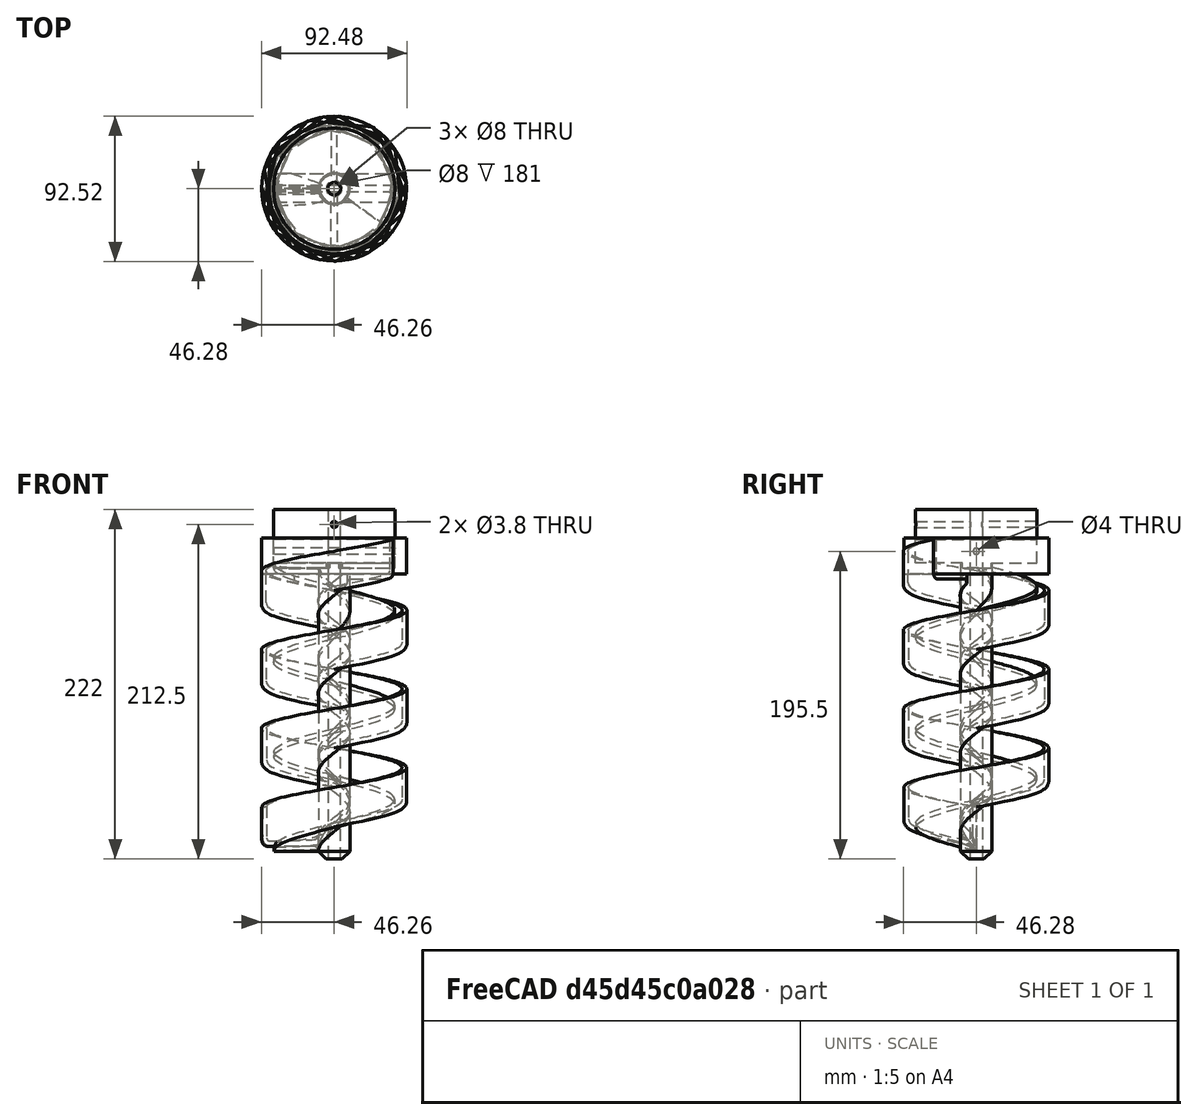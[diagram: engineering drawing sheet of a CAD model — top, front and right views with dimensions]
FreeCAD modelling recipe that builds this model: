
FCSTD DOCUMENT  (FreeCAD 1.1R14555 (Git shallow))
Label: Body - 1.4
License: All rights reserved
LicenseURL: https://en.wikipedia.org/wiki/All_rights_reserved
objects: Sketcher::SketchObject×13, PartDesign::Pad×7, PartDesign::Chamfer×6, PartDesign::Pocket×5, PartDesign::AdditiveHelix×2, PartDesign::Body×2, App::Point×2, PartDesign::Fillet×1
note: 91 computed .brp shape members not serialized (recipe doc carries the construction recipe); baked Part::Feature solids carry a one-line shape summary decoded from their .brp

FEATURE [Sketcher::SketchObject] Sketch
  ArcFitTolerance = 1e-06
  AttachmentSupport = -> [XY_Plane]
  ExternalTypes = [0]
  FullyConstrained = true
  MakeInternals = false
  MapMode = 5
  sketch-geometry (1):
    g0: Circle CenterX=0 CenterY=0 CenterZ=0 NormalX=0 NormalY=0 NormalZ=1 AngleXU=0 Radius=10
  constraints (2):
    c: Coincident(g0,g-1)
    c: Diameter(g0) = 20
FEATURE [PartDesign::Pad] Pad
  Direction = (0,0,1)
  Length = 200
  Length2 = 10
  Profile = -> Sketch
  ReferenceAxis = -> Sketch [N_Axis]
  Refine = true
  SideType = 0
  Suppressed = false
  Type = 0
  Type2 = 0
FEATURE [PartDesign::Chamfer] Chamfer
  Angle = 45
  Base = -> Pad [Edge2]
  BaseFeature = -> Pad
  ChamferType = 0
  FlipDirection = false
  Refine = true
  Size = 5
  Size2 = 1
  SupportTransform = false
  Suppressed = false
  UseAllEdges = false
FEATURE [Sketcher::SketchObject] Sketch001
  ArcFitTolerance = 1e-06
  AttachmentSupport = -> [XZ_Plane]
  ExternalGeometry = -> [Chamfer]
  ExternalTypes = [0]
  FullyConstrained = true
  MakeInternals = false
  MapMode = 5
  Placement = pos=(0,0,0) rot=(1,0,0;1.5708rad)
  expr: Constraints[11] = 77 / 2 - 0.3
  sketch-geometry (4):
    g0: LineSegment StartX=-38.2 StartY=8 StartZ=0 EndX=-38.2 EndY=5 EndZ=0
    g1: LineSegment StartX=-38.2 StartY=5 StartZ=0 EndX=0 EndY=5 EndZ=0
    g2: LineSegment StartX=0 StartY=5 StartZ=0 EndX=0 EndY=8 EndZ=0
    g3: LineSegment StartX=0 StartY=8 StartZ=0 EndX=-38.2 EndY=8 EndZ=0
  constraints (12):
    c: Coincident(g0,g1)
    c: Coincident(g1,g2)
    c: Coincident(g2,g3)
    c: Coincident(g3,g0)
    c: Vertical(g0)
    c: Vertical(g2)
    c: Horizontal(g1)
    c: Horizontal(g3)
    c: PointOnObject(g1,g-2)
    c: Horizontal(g0,g-3)
    c: DistanceY(g0,g0) = 3
    c: DistanceX(g1,g1) = 38.2
FEATURE [PartDesign::AdditiveHelix] AdditiveHelix
  Angle = 0.1
  Axis = (0,2e-16,1)
  Base = (0,0,0)
  BaseFeature = -> Chamfer
  Growth = 0.10472
  HasBeenEdited = true
  Height = 180
  LeftHanded = false
  Mode = 0
  Outside = false
  Pitch = 60
  Profile = -> Sketch001
  ReferenceAxis = -> Sketch001 [V_Axis]
  Refine = true
  Suppressed = false
  Tolerance = 0.1
  Turns = 3
FEATURE [Sketcher::SketchObject] Sketch002
  ArcFitTolerance = 1e-06
  AttachmentSupport = -> [Chamfer]
  ExternalTypes = [0]
  FullyConstrained = true
  MakeInternals = false
  MapMode = 5
  Placement = pos=(0,0,200) rot=(0,0,1;0rad)
  sketch-geometry (1):
    g0: Circle CenterX=0 CenterY=0 CenterZ=0 NormalX=0 NormalY=0 NormalZ=1 AngleXU=0 Radius=38.5
  constraints (2):
    c: Coincident(g0,g-1)
    c: Diameter(g0) = 77
FEATURE [PartDesign::Chamfer] Chamfer001
  Angle = 45
  Base = -> AdditiveHelix [Edge12]
  BaseFeature = -> AdditiveHelix
  ChamferType = 0
  FlipDirection = false
  Refine = true
  Size = 2.99
  Size2 = 1
  SupportTransform = false
  Suppressed = false
  UseAllEdges = false
FEATURE [PartDesign::Chamfer] Chamfer002
  Angle = 45
  Base = -> Chamfer001 [Edge12]
  BaseFeature = -> Chamfer001
  ChamferType = 0
  FlipDirection = false
  Refine = true
  Size = 4
  Size2 = 1
  SupportTransform = false
  Suppressed = false
  UseAllEdges = false
FEATURE [PartDesign::Chamfer] Chamfer003
  Angle = 45
  Base = -> Chamfer002 [Edge13]
  BaseFeature = -> Chamfer002
  ChamferType = 0
  FlipDirection = false
  Refine = true
  Size = 4
  Size2 = 1
  SupportTransform = false
  Suppressed = false
  UseAllEdges = false
FEATURE [PartDesign::Pad] Pad001
  BaseFeature = -> Chamfer003
  Direction = (0,0,1)
  Length = 3
  Length2 = 10
  Profile = -> Sketch002
  ReferenceAxis = -> Sketch002 [N_Axis]
  Refine = true
  SideType = 0
  Suppressed = false
  Type = 0
  Type2 = 0
FEATURE [Sketcher::SketchObject] Sketch003
  ArcFitTolerance = 1e-06
  AttachmentSupport = -> [Pad001]
  ExternalTypes = [0]
  FullyConstrained = true
  MakeInternals = false
  MapMode = 5
  Placement = pos=(0,0,200) rot=(1,0,0;3.14159rad)
  sketch-geometry (1):
    g0: Circle CenterX=0 CenterY=0 CenterZ=0 NormalX=0 NormalY=0 NormalZ=1 AngleXU=0 Radius=38.5
  constraints (2):
    c: Coincident(g0,g-1)
    c: Diameter(g0) = 77
FEATURE [PartDesign::Pad] Pad002
  BaseFeature = -> Pad001
  Direction = (0,0,-1)
  Length = 12
  Length2 = 10
  Profile = -> Sketch003
  ReferenceAxis = -> Sketch003 [N_Axis]
  Refine = true
  SideType = 0
  Suppressed = false
  Type = 0
  Type2 = 0
FEATURE [PartDesign::Fillet] Fillet
  Base = -> Pad002 [Edge36]
  BaseFeature = -> Pad002
  Radius = 3
  Refine = true
  SupportTransform = false
  Suppressed = false
  UseAllEdges = false
FEATURE [Sketcher::SketchObject] Sketch004
  ArcFitTolerance = 1e-06
  AttachmentSupport = -> [Fillet]
  ExternalTypes = [0]
  FullyConstrained = true
  MakeInternals = false
  MapMode = 5
  Placement = pos=(0,0,203) rot=(0,0,1;0rad)
  sketch-geometry (2):
    g0: Circle CenterX=0 CenterY=0 CenterZ=0 NormalX=0 NormalY=0 NormalZ=1 AngleXU=0 Radius=38.5
    g1: Circle CenterX=0 CenterY=0 CenterZ=0 NormalX=0 NormalY=0 NormalZ=1 AngleXU=0 Radius=50
  constraints (4):
    c: Coincident(g0,g-1)
    c: Diameter(g0) = 77
    c: Coincident(g1,g0)
    c: Diameter(g1) = 100
FEATURE [PartDesign::Pocket] Pocket
  BaseFeature = -> Fillet
  Direction = (0,0,-1)
  Length = 180
  Length2 = 5
  Profile = -> Sketch004
  ReferenceAxis = -> Sketch004 [N_Axis]
  Refine = true
  Reversed = true
  SideType = 0
  Suppressed = false
  Type = 0
  Type2 = 0
FEATURE [Sketcher::SketchObject] Sketch005
  ArcFitTolerance = 1e-06
  AttachmentSupport = -> [YZ_Plane]
  ExternalGeometry = -> [Pocket]
  ExternalTypes = [0]
  FullyConstrained = true
  MakeInternals = false
  MapMode = 5
  Placement = pos=(0,0,0) rot=(0.57735,0.57735,0.57735;2.0944rad)
  sketch-geometry (1):
    g0: Circle CenterX=9.4e-15 CenterY=195.5 CenterZ=0 NormalX=0 NormalY=0 NormalZ=1 AngleXU=0 Radius=2
  constraints (3):
    c: PointOnObject(g0,g-3)
    c: Diameter(g0) = 4
    c: Symmetric(g-3,g-3,g0)
FEATURE [PartDesign::Pocket] Pocket001
  BaseFeature = -> Pocket
  Direction = (-1,0,0)
  Length = 500
  Length2 = 5
  Profile = -> Sketch005
  ReferenceAxis = -> Sketch005 [N_Axis]
  Refine = true
  Reversed = true
  SideType = 0
  Suppressed = false
  Type = 0
  Type2 = 0
FEATURE [PartDesign::Pocket] Pocket002
  BaseFeature = -> Pocket001
  Direction = (-1,0,0)
  Length = 5
  Length2 = 5
  Profile = -> Pocket001 [Face21]
  Refine = true
  SideType = 0
  Suppressed = false
  Type = 1
  Type2 = 0
FEATURE [Sketcher::SketchObject] Sketch006
  ArcFitTolerance = 1e-06
  AttachmentSupport = -> [YZ_Plane]
  ExternalTypes = [0]
  FullyConstrained = false
  MakeInternals = false
  MapMode = 5
  Placement = pos=(0,0,0) rot=(0.57735,0.57735,0.57735;2.0944rad)
  sketch-geometry (4):
    g0: LineSegment StartX=9.56195 StartY=192.563 StartZ=0 EndX=-8.62475 EndY=192.563 EndZ=0
    g1: LineSegment StartX=-8.62475 StartY=192.563 StartZ=0 EndX=-8.62475 EndY=184.759 EndZ=0
    g2: LineSegment StartX=-8.62475 StartY=184.759 StartZ=0 EndX=9.56195 EndY=184.759 EndZ=0
    g3: LineSegment StartX=9.56195 StartY=184.759 StartZ=0 EndX=9.56195 EndY=192.563 EndZ=0
  constraints (8):
    c: Coincident(g0,g1)
    c: Coincident(g1,g2)
    c: Coincident(g2,g3)
    c: Coincident(g3,g0)
    c: Horizontal(g0)
    c: Horizontal(g2)
    c: Vertical(g1)
    c: Vertical(g3)
FEATURE [PartDesign::Pad] Pad003
  BaseFeature = -> Pocket002
  Direction = (1,0,0)
  Length = 50
  Length2 = 50
  Profile = -> Sketch006
  ReferenceAxis = -> Sketch006 [N_Axis]
  Refine = true
  SideType = 0
  Suppressed = false
  Type = 4
  Type2 = 0
FEATURE [Sketcher::SketchObject] Sketch007
  ArcFitTolerance = 1e-06
  AttachmentSupport = -> [Pad003]
  ExternalTypes = [0]
  FullyConstrained = true
  MakeInternals = false
  MapMode = 5
  Placement = pos=(0,0,203) rot=(0,0,1;0rad)
  sketch-geometry (2):
    g0: Circle CenterX=0 CenterY=0 CenterZ=0 NormalX=0 NormalY=0 NormalZ=1 AngleXU=0 Radius=38.5
    g1: Circle CenterX=0 CenterY=0 CenterZ=0 NormalX=0 NormalY=0 NormalZ=1 AngleXU=0 Radius=55
  constraints (4):
    c: Coincident(g0,g-1)
    c: Diameter(g0) = 77
    c: Diameter(g1) = 110
    c: Coincident(g1,g0)
FEATURE [PartDesign::Pocket] Pocket003
  BaseFeature = -> Pad003
  Direction = (0,0,-1)
  Length = 30
  Length2 = 5
  Profile = -> Sketch007
  ReferenceAxis = -> Sketch007 [N_Axis]
  Refine = true
  SideType = 0
  Suppressed = false
  Type = 0
  Type2 = 0
FEATURE [PartDesign::Body] Body
  AllowCompound = false
  Group = -> [Sketch,Pad,Chamfer,Sketch001,AdditiveHelix,Sketch002,Chamfer001,Chamfer002,Chamfer003,Pad001,Sketch003,Pad002,Fillet,Sketch004,Pocket,Sketch005,Pocket001,Pocket002,Sketch006,Pad003,Sketch007,Pocket003]
  Origin = -> Origin
  Tip = -> Pocket003
FEATURE [Sketcher::SketchObject] Sketch008
  ArcFitTolerance = 1e-06
  AttachmentSupport = -> [XY_Plane001]
  ExternalTypes = [0]
  FullyConstrained = true
  MakeInternals = false
  MapMode = 5
  sketch-geometry (2):
    g0: Circle CenterX=0 CenterY=0 CenterZ=0 NormalX=0 NormalY=0 NormalZ=1 AngleXU=0 Radius=10
    g1: Circle CenterX=0 CenterY=0 CenterZ=0 NormalX=0 NormalY=0 NormalZ=1 AngleXU=0 Radius=4
  constraints (4):
    c: Coincident(g0,g-1)
    c: Diameter(g0) = 20
    c: Coincident(g1,g0)
    c: Diameter(g1) = 8
FEATURE [PartDesign::Pad] Pad004
  Direction = (0,0,1)
  Length = 200
  Length2 = 10
  Profile = -> Sketch008
  ReferenceAxis = -> Sketch008 [N_Axis]
  Refine = true
  SideType = 0
  Suppressed = false
  Type = 0
  Type2 = 0
FEATURE [PartDesign::Chamfer] Chamfer004
  Angle = 45
  Base = -> Pad004 [Edge2]
  BaseFeature = -> Pad004
  ChamferType = 0
  FlipDirection = false
  Refine = true
  Size = 5
  Size2 = 1
  SupportTransform = false
  Suppressed = false
  UseAllEdges = false
FEATURE [Sketcher::SketchObject] Sketch009
  ArcFitTolerance = 1e-06
  AttachmentSupport = -> [XZ_Plane001]
  ExternalGeometry = -> [Chamfer004]
  ExternalTypes = [0]
  FullyConstrained = true
  MakeInternals = false
  MapMode = 5
  Placement = pos=(0,0,0) rot=(1,0,0;1.5708rad)
  sketch-geometry (13):
    g0: LineSegment StartX=-13 StartY=11 StartZ=0 EndX=-41 EndY=11 EndZ=0
    g1: LineSegment StartX=-46 StartY=12 StartZ=0 EndX=-46 EndY=33 EndZ=0
    g2: LineSegment StartX=-43 StartY=33 StartZ=0 EndX=-43 EndY=13 EndZ=0
    g3: ArcOfCircle CenterX=-41 CenterY=13 CenterZ=0 NormalX=0 NormalY=0 NormalZ=1 AngleXU=0 Radius=2 StartAngle=3.14159 EndAngle=4.71239
    g4: GeomPoint [constr] X=-43 Y=11 Z=0
    g5: ArcOfCircle CenterX=-42 CenterY=12 CenterZ=0 NormalX=0 NormalY=0 NormalZ=1 AngleXU=0 Radius=4 StartAngle=3.14159 EndAngle=4.71239
    g6: ArcOfCircle CenterX=-13 CenterY=14 CenterZ=0 NormalX=0 NormalY=0 NormalZ=1 AngleXU=0 Radius=3 StartAngle=4.71239 EndAngle=6.28319
    g7: LineSegment StartX=-10 StartY=14 StartZ=0 EndX=-8 EndY=14 EndZ=0
    g8: LineSegment StartX=-8 StartY=14 StartZ=0 EndX=-8 EndY=5 EndZ=0
    g9: LineSegment StartX=-46 StartY=33 StartZ=0 EndX=-43 EndY=33 EndZ=0
    g10: LineSegment StartX=-42 StartY=8 StartZ=0 EndX=-13 EndY=8 EndZ=0
    g11: ArcOfCircle CenterX=-13 CenterY=5 CenterZ=0 NormalX=0 NormalY=0 NormalZ=1 AngleXU=0 Radius=3 StartAngle=1e-16 EndAngle=1.5708
    g12: LineSegment StartX=-10 StartY=5 StartZ=0 EndX=-8 EndY=5 EndZ=0
  constraints (38):
    c: Vertical(g1)
    c: Vertical(g2)
    c: PointOnObject(g4,g0)
    c: PointOnObject(g4,g2)
    c: Tangent(g0,g3) = 1.5708
    c: Tangent(g2,g3) = -1.5708
    c: Tangent(g1,g5) = 1.5708
    c: DistanceY(g2,g2) = 20
    c: Radius(g3) = 2
    c: Radius(g5) = 4
    c: Horizontal(g0)
    c: DistanceX(g1,g-1) = 46
    c: Coincident(g6,g0)
    c: Vertical(g6,g0)
    c: Radius(g6) = 3
    c: Horizontal(g6,g6)
    c: DistanceY(g5,g0) = 3
    c: Coincident(g7,g6)
    c: Coincident(g8,g7)
    c: Vertical(g8)
    c: Horizontal(g7)
    c: Distance(g7,g7) = 2
    c: Horizontal(g1,g2)
    c: DistanceX(g1,g2) = 3
    c: Coincident(g9,g1)
    c: Coincident(g9,g2)
    c: Vertical(g6,g-3)
    c: Vertical(g5,g5)
    c: Coincident(g10,g5)
    c: Horizontal(g10)
    c: Coincident(g11,g10)
    c: Coincident(g11,g-3)
    c: Vertical(g10,g11)
    c: Horizontal(g11,g11)
    c: Coincident(g12,g11)
    c: Coincident(g12,g8)
    c: Horizontal(g12)
    c: Equal(g6,g11)
FEATURE [PartDesign::AdditiveHelix] AdditiveHelix001
  Angle = 0.1
  Axis = (0,2e-16,1)
  Base = (0,0,0)
  BaseFeature = -> Chamfer004
  Growth = 0.0872666
  HasBeenEdited = true
  Height = 170
  LeftHanded = false
  Mode = 0
  Outside = false
  Pitch = 50
  Profile = -> Sketch009
  ReferenceAxis = -> Sketch009 [V_Axis]
  Refine = true
  Suppressed = false
  Tolerance = 0.1
  Turns = 3.4
FEATURE [App::Point] Origin002  label="Origin"
  Role = Origin
FEATURE [App::Point] Origin003  label="Origin"
  Role = Origin
FEATURE [Sketcher::SketchObject] Sketch010
  ArcFitTolerance = 1e-06
  AttachmentSupport = -> [AdditiveHelix001]
  ExternalTypes = [0]
  FullyConstrained = true
  MakeInternals = false
  MapMode = 5
  Placement = pos=(0,0,200) rot=(0,0,1;0rad)
  expr: Constraints[3] = 2 * 46
  sketch-geometry (2):
    g0: Circle CenterX=0 CenterY=0 CenterZ=0 NormalX=0 NormalY=0 NormalZ=1 AngleXU=0 Radius=4
    g1: Circle CenterX=0 CenterY=0 CenterZ=0 NormalX=0 NormalY=0 NormalZ=1 AngleXU=0 Radius=46
  constraints (4):
    c: Coincident(g0,g-1)
    c: Coincident(g1,g0)
    c: Diameter(g0) = 8
    c: Diameter(g1) = 92
FEATURE [PartDesign::Pad] Pad005
  BaseFeature = -> AdditiveHelix001
  Direction = (0,0,1)
  Length = 19
  Length2 = 4
  Profile = -> Sketch010
  ReferenceAxis = -> Sketch010 [N_Axis]
  Reversed = true
  SideType = 1
  Suppressed = false
  Type = 0
  Type2 = 0
FEATURE [Sketcher::SketchObject] Sketch013
  ArcFitTolerance = 1e-06
  ExternalTypes = [0]
  FullyConstrained = true
  MakeInternals = false
  MapMode = 5
  Placement = pos=(0,0,204) rot=(0,0,1;0rad)
  sketch-geometry (2):
    g0: Circle CenterX=0 CenterY=0 CenterZ=0 NormalX=0 NormalY=0 NormalZ=1 AngleXU=0 Radius=38.5
    g1: Circle CenterX=0 CenterY=0 CenterZ=0 NormalX=0 NormalY=0 NormalZ=1 AngleXU=0 Radius=4
  constraints (4):
    c: Coincident(g0,g-1)
    c: Diameter(g0) = 77
    c: Coincident(g1,g0)
    c: Diameter(g1) = 8
FEATURE [PartDesign::Pad] Pad006
  BaseFeature = -> Pad005
  Direction = (0,0,1)
  Length = 18
  Length2 = 10
  Profile = -> Sketch013
  ReferenceAxis = -> Sketch013 [N_Axis]
  SideType = 0
  Suppressed = false
  Type = 0
  Type2 = 0
FEATURE [Sketcher::SketchObject] Sketch014
  ArcFitTolerance = 1e-06
  AttachmentSupport = -> [Origin001]
  ExternalTypes = [0]
  FullyConstrained = true
  MakeInternals = false
  MapMode = 5
  Placement = pos=(0,0,0) rot=(1,0,0;1.5708rad)
  sketch-geometry (1):
    g0: Circle CenterX=0 CenterY=212.5 CenterZ=0 NormalX=0 NormalY=0 NormalZ=1 AngleXU=0 Radius=1.9
  constraints (3):
    c: PointOnObject(g0,g-2)
    c: Diameter(g0) = 3.8
    c: Distance(g0,g-1) = 212.5
FEATURE [PartDesign::Pocket] Pocket004
  BaseFeature = -> Pad006
  Direction = (0,1,0)
  Length = 60
  Length2 = 60
  Profile = -> Sketch014
  ReferenceAxis = -> Sketch014 [N_Axis]
  SideType = 1
  Suppressed = false
  Type = 0
  Type2 = 0
FEATURE [PartDesign::Chamfer] Chamfer005
  Angle = 45
  Base = -> Pocket004 [Edge14]
  BaseFeature = -> Pocket004
  ChamferType = 0
  FlipDirection = false
  Size = 2.5
  Size2 = 1
  SupportTransform = false
  Suppressed = false
  UseAllEdges = false
FEATURE [PartDesign::Body] Body001
  AllowCompound = false
  Group = -> [Sketch008,Pad004,Chamfer004,Sketch009,AdditiveHelix001,Sketch010,Pad005,Sketch013,Pad006,Sketch014,Pocket004,Chamfer005]
  Origin = -> Origin001
  Tip = -> Chamfer005
